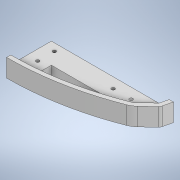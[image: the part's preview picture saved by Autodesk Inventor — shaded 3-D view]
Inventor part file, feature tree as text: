
AUTODESK INVENTOR PART (.ipt)
format: ipt  version: 2020 (Build 240168000, 168)  size: 267,264 bytes
history: native  units: mm
features: sketch x3, extrude x3, hole x2, fillet x2
ambient origin geometry x8: Origin, YZ Plane, XZ Plane, XY Plane, X Axis, Y Axis, Z Axis, Center Point
bodies: Body1 (feature_tree)
feature tree (10):
  sketch  "스케치1"
  extrude  "돌출20"  Depth=657.5mm
  extrude  "돌출21"  Depth=585.0mm
  sketch  "스케치22"
  extrude  "돌출23"  Depth=0.872665mm
  hole  "구멍5"  [1 undecoded]
  hole  "구멍6"  [1 undecoded]
  fillet  "모깎기1"  Radius=999.812583mm
  fillet  "모깎기2"  Radius=2.094395mm
  sketch  "스케치23"
note: 2 required parameter values undecoded (feature->parameter linkage not recoverable at this tier; creation-order binding heuristic only, values carry confidence <= 0.55)
